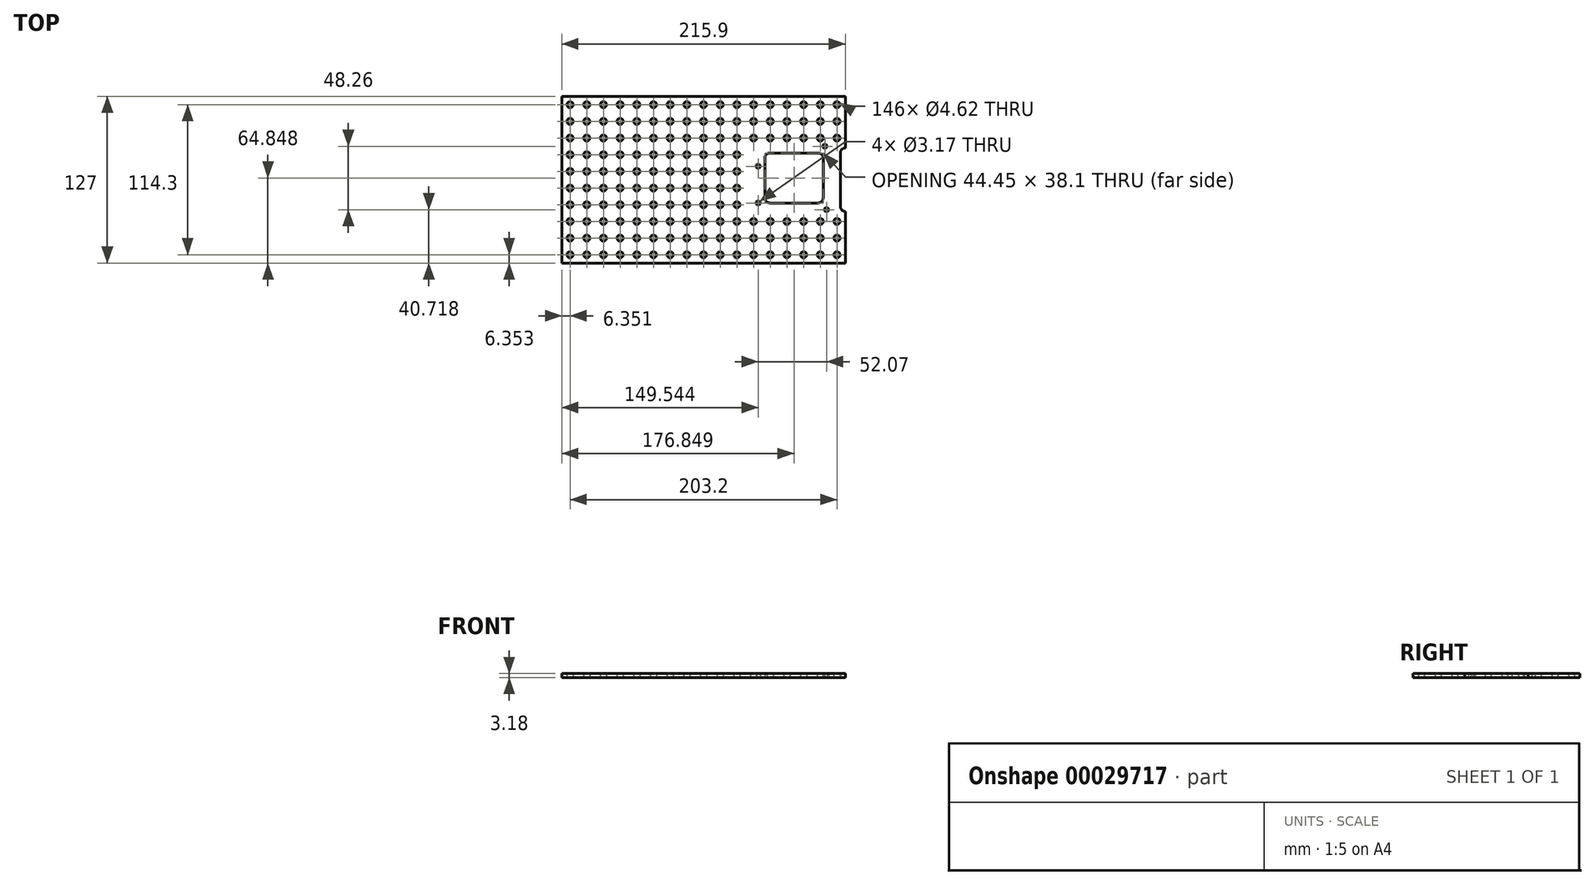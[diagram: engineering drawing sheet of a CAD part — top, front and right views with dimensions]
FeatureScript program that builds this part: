
annotation { "Feature Type Name" : "Feature", "Feature Type Description" : "" }
export const myFeature = defineFeature(function(context is Context, id is Id, definition is map)
    precondition{}
    {
        {
            var Q0;
            Q0=qCreatedBy(makeId("Top.planeOp"),FACE);
            var sketch = newSketch(context, id + "F0", { "sketchPlane" : qUnion([Q0])});
            skLineSegment(sketch, "E0.bottom", {"start": v(-98.48, 59.36) * mm, "end": v(117.42, 59.36) * mm});
            skLineSegment(sketch, "E0.top", {"start": v(-98.48, -67.64) * mm, "end": v(113.61, -67.64) * mm});
            skLineSegment(sketch, "E0.left", {"start": v(-98.48, 59.36) * mm, "end": v(-98.48, -67.64) * mm});
            skLineSegment(sketch, "E0.right", {"start": v(117.42, 59.36) * mm, "end": v(117.42, -63.83) * mm});
            skCircle(sketch, "E1.MirrorC", {"center": v(51.06, -21.84) * mm, "radius": 1.59 * mm});
            skCircle(sketch, "E2.MirrorC", {"center": v(51.06, 6.1) * mm, "radius": 1.59 * mm});
            skCircle(sketch, "E3.MirrorC", {"center": v(103.13, -26.92) * mm, "radius": 1.59 * mm});
            skCircle(sketch, "E4.MirrorC", {"center": v(101.86, 21.34) * mm, "radius": 1.59 * mm});
            skCircle(sketch, "E5", {"center": v(-92.13, 53.01) * mm, "radius": 2.31 * mm});
            skCircle(sketch, "E6.1.0.0", {"center": v(-79.43, 53.01) * mm, "radius": 2.31 * mm});
            skCircle(sketch, "E6.2.0.0", {"center": v(-66.73, 53.01) * mm, "radius": 2.31 * mm});
            skCircle(sketch, "E6.3.0.0", {"center": v(-54.03, 53.01) * mm, "radius": 2.31 * mm});
            skCircle(sketch, "E6.4.0.0", {"center": v(-41.33, 53.01) * mm, "radius": 2.31 * mm});
            skCircle(sketch, "E6.5.0.0", {"center": v(-28.63, 53.01) * mm, "radius": 2.31 * mm});
            skCircle(sketch, "E6.6.0.0", {"center": v(-15.93, 53.01) * mm, "radius": 2.31 * mm});
            skCircle(sketch, "E6.7.0.0", {"center": v(-3.23, 53.01) * mm, "radius": 2.31 * mm});
            skCircle(sketch, "E6.8.0.0", {"center": v(9.47, 53.01) * mm, "radius": 2.31 * mm});
            skCircle(sketch, "E6.9.0.0", {"center": v(22.17, 53.01) * mm, "radius": 2.31 * mm});
            skLineSegment(sketch, "E6.direction1", {"start": v(-92.13, 53.01) * mm, "end": v(-79.43, 53.01) * mm, "construction": true});
            skCircle(sketch, "E7.1.0.0", {"center": v(-92.13, 40.31) * mm, "radius": 2.31 * mm});
            skCircle(sketch, "E7.1.0.1", {"center": v(-79.43, 40.31) * mm, "radius": 2.31 * mm});
            skCircle(sketch, "E7.1.0.2", {"center": v(-66.73, 40.31) * mm, "radius": 2.31 * mm});
            skCircle(sketch, "E7.1.0.3", {"center": v(-3.23, 40.31) * mm, "radius": 2.31 * mm});
            skCircle(sketch, "E7.1.0.4", {"center": v(-15.93, 40.31) * mm, "radius": 2.31 * mm});
            skCircle(sketch, "E7.1.0.5", {"center": v(22.17, 40.31) * mm, "radius": 2.31 * mm});
            skCircle(sketch, "E7.1.0.6", {"center": v(-28.63, 40.31) * mm, "radius": 2.31 * mm});
            skCircle(sketch, "E7.1.0.7", {"center": v(-41.33, 40.31) * mm, "radius": 2.31 * mm});
            skCircle(sketch, "E7.1.0.8", {"center": v(9.47, 40.31) * mm, "radius": 2.31 * mm});
            skLineSegment(sketch, "E7.1.0.9", {"start": v(-92.13, 40.31) * mm, "end": v(-79.43, 40.31) * mm, "construction": true});
            skCircle(sketch, "E7.1.0.10", {"center": v(-54.03, 40.31) * mm, "radius": 2.31 * mm});
            skCircle(sketch, "E7.2.0.0", {"center": v(-92.13, 27.61) * mm, "radius": 2.31 * mm});
            skCircle(sketch, "E7.2.0.1", {"center": v(-79.43, 27.61) * mm, "radius": 2.31 * mm});
            skCircle(sketch, "E7.2.0.2", {"center": v(-66.73, 27.61) * mm, "radius": 2.31 * mm});
            skCircle(sketch, "E7.2.0.3", {"center": v(-3.23, 27.61) * mm, "radius": 2.31 * mm});
            skCircle(sketch, "E7.2.0.4", {"center": v(-15.93, 27.61) * mm, "radius": 2.31 * mm});
            skCircle(sketch, "E7.2.0.5", {"center": v(22.17, 27.61) * mm, "radius": 2.31 * mm});
            skCircle(sketch, "E7.2.0.6", {"center": v(-28.63, 27.61) * mm, "radius": 2.31 * mm});
            skCircle(sketch, "E7.2.0.7", {"center": v(-41.33, 27.61) * mm, "radius": 2.31 * mm});
            skCircle(sketch, "E7.2.0.8", {"center": v(9.47, 27.61) * mm, "radius": 2.31 * mm});
            skLineSegment(sketch, "E7.2.0.9", {"start": v(-92.13, 27.61) * mm, "end": v(-79.43, 27.61) * mm, "construction": true});
            skCircle(sketch, "E7.2.0.10", {"center": v(-54.03, 27.61) * mm, "radius": 2.31 * mm});
            skCircle(sketch, "E7.3.0.0", {"center": v(-92.13, 14.91) * mm, "radius": 2.31 * mm});
            skCircle(sketch, "E7.3.0.1", {"center": v(-79.43, 14.91) * mm, "radius": 2.31 * mm});
            skCircle(sketch, "E7.3.0.2", {"center": v(-66.73, 14.91) * mm, "radius": 2.31 * mm});
            skCircle(sketch, "E7.3.0.3", {"center": v(-3.23, 14.91) * mm, "radius": 2.31 * mm});
            skCircle(sketch, "E7.3.0.4", {"center": v(-15.93, 14.91) * mm, "radius": 2.31 * mm});
            skCircle(sketch, "E7.3.0.5", {"center": v(22.17, 14.91) * mm, "radius": 2.31 * mm});
            skCircle(sketch, "E7.3.0.6", {"center": v(-28.63, 14.91) * mm, "radius": 2.31 * mm});
            skCircle(sketch, "E7.3.0.7", {"center": v(-41.33, 14.91) * mm, "radius": 2.31 * mm});
            skCircle(sketch, "E7.3.0.8", {"center": v(9.47, 14.91) * mm, "radius": 2.31 * mm});
            skLineSegment(sketch, "E7.3.0.9", {"start": v(-92.13, 14.91) * mm, "end": v(-79.43, 14.91) * mm, "construction": true});
            skCircle(sketch, "E7.3.0.10", {"center": v(-54.03, 14.91) * mm, "radius": 2.31 * mm});
            skCircle(sketch, "E7.4.0.0", {"center": v(-92.13, 2.21) * mm, "radius": 2.31 * mm});
            skCircle(sketch, "E7.4.0.1", {"center": v(-79.43, 2.21) * mm, "radius": 2.31 * mm});
            skCircle(sketch, "E7.4.0.2", {"center": v(-66.73, 2.21) * mm, "radius": 2.31 * mm});
            skCircle(sketch, "E7.4.0.3", {"center": v(-3.23, 2.21) * mm, "radius": 2.31 * mm});
            skCircle(sketch, "E7.4.0.4", {"center": v(-15.93, 2.21) * mm, "radius": 2.31 * mm});
            skCircle(sketch, "E7.4.0.5", {"center": v(22.17, 2.21) * mm, "radius": 2.31 * mm});
            skCircle(sketch, "E7.4.0.6", {"center": v(-28.63, 2.21) * mm, "radius": 2.31 * mm});
            skCircle(sketch, "E7.4.0.7", {"center": v(-41.33, 2.21) * mm, "radius": 2.31 * mm});
            skCircle(sketch, "E7.4.0.8", {"center": v(9.47, 2.21) * mm, "radius": 2.31 * mm});
            skLineSegment(sketch, "E7.4.0.9", {"start": v(-92.13, 2.21) * mm, "end": v(-79.43, 2.21) * mm, "construction": true});
            skCircle(sketch, "E7.4.0.10", {"center": v(-54.03, 2.21) * mm, "radius": 2.31 * mm});
            skCircle(sketch, "E7.5.0.0", {"center": v(-92.13, -10.49) * mm, "radius": 2.31 * mm});
            skCircle(sketch, "E7.5.0.1", {"center": v(-79.43, -10.49) * mm, "radius": 2.31 * mm});
            skCircle(sketch, "E7.5.0.2", {"center": v(-66.73, -10.49) * mm, "radius": 2.31 * mm});
            skCircle(sketch, "E7.5.0.3", {"center": v(-3.23, -10.49) * mm, "radius": 2.31 * mm});
            skCircle(sketch, "E7.5.0.4", {"center": v(-15.93, -10.49) * mm, "radius": 2.31 * mm});
            skCircle(sketch, "E7.5.0.5", {"center": v(22.17, -10.49) * mm, "radius": 2.31 * mm});
            skCircle(sketch, "E7.5.0.6", {"center": v(-28.63, -10.49) * mm, "radius": 2.31 * mm});
            skCircle(sketch, "E7.5.0.7", {"center": v(-41.33, -10.49) * mm, "radius": 2.31 * mm});
            skCircle(sketch, "E7.5.0.8", {"center": v(9.47, -10.49) * mm, "radius": 2.31 * mm});
            skLineSegment(sketch, "E7.5.0.9", {"start": v(-92.13, -10.49) * mm, "end": v(-79.43, -10.49) * mm, "construction": true});
            skCircle(sketch, "E7.5.0.10", {"center": v(-54.03, -10.49) * mm, "radius": 2.31 * mm});
            skCircle(sketch, "E7.6.0.0", {"center": v(-92.13, -23.19) * mm, "radius": 2.31 * mm});
            skCircle(sketch, "E7.6.0.1", {"center": v(-79.43, -23.19) * mm, "radius": 2.31 * mm});
            skCircle(sketch, "E7.6.0.2", {"center": v(-66.73, -23.19) * mm, "radius": 2.31 * mm});
            skCircle(sketch, "E7.6.0.3", {"center": v(-3.23, -23.19) * mm, "radius": 2.31 * mm});
            skCircle(sketch, "E7.6.0.4", {"center": v(-15.93, -23.19) * mm, "radius": 2.31 * mm});
            skCircle(sketch, "E7.6.0.5", {"center": v(22.17, -23.19) * mm, "radius": 2.31 * mm});
            skCircle(sketch, "E7.6.0.6", {"center": v(-28.63, -23.19) * mm, "radius": 2.31 * mm});
            skCircle(sketch, "E7.6.0.7", {"center": v(-41.33, -23.19) * mm, "radius": 2.31 * mm});
            skCircle(sketch, "E7.6.0.8", {"center": v(9.47, -23.19) * mm, "radius": 2.31 * mm});
            skLineSegment(sketch, "E7.6.0.9", {"start": v(-92.13, -23.19) * mm, "end": v(-79.43, -23.19) * mm, "construction": true});
            skCircle(sketch, "E7.6.0.10", {"center": v(-54.03, -23.19) * mm, "radius": 2.31 * mm});
            skCircle(sketch, "E7.7.0.0", {"center": v(-92.13, -35.89) * mm, "radius": 2.31 * mm});
            skCircle(sketch, "E7.7.0.1", {"center": v(-79.43, -35.89) * mm, "radius": 2.31 * mm});
            skCircle(sketch, "E7.7.0.2", {"center": v(-66.73, -35.89) * mm, "radius": 2.31 * mm});
            skCircle(sketch, "E7.7.0.3", {"center": v(-3.23, -35.89) * mm, "radius": 2.31 * mm});
            skCircle(sketch, "E7.7.0.4", {"center": v(-15.93, -35.89) * mm, "radius": 2.31 * mm});
            skCircle(sketch, "E7.7.0.5", {"center": v(22.17, -35.89) * mm, "radius": 2.31 * mm});
            skCircle(sketch, "E7.7.0.6", {"center": v(-28.63, -35.89) * mm, "radius": 2.31 * mm});
            skCircle(sketch, "E7.7.0.7", {"center": v(-41.33, -35.89) * mm, "radius": 2.31 * mm});
            skCircle(sketch, "E7.7.0.8", {"center": v(9.47, -35.89) * mm, "radius": 2.31 * mm});
            skLineSegment(sketch, "E7.7.0.9", {"start": v(-92.13, -35.89) * mm, "end": v(-79.43, -35.89) * mm, "construction": true});
            skCircle(sketch, "E7.7.0.10", {"center": v(-54.03, -35.89) * mm, "radius": 2.31 * mm});
            skLineSegment(sketch, "E7.direction1", {"start": v(-92.13, 53.01) * mm, "end": v(-92.13, 40.31) * mm, "construction": true});
            skCircle(sketch, "E8.0.8.0", {"center": v(-92.13, -48.59) * mm, "radius": 2.31 * mm});
            skCircle(sketch, "E8.2.8.0", {"center": v(-79.43, -48.59) * mm, "radius": 2.31 * mm});
            skCircle(sketch, "E8.4.8.0", {"center": v(-66.73, -48.59) * mm, "radius": 2.31 * mm});
            skCircle(sketch, "E8.6.8.0", {"center": v(-3.23, -48.59) * mm, "radius": 2.31 * mm});
            skCircle(sketch, "E8.8.8.0", {"center": v(-15.93, -48.59) * mm, "radius": 2.31 * mm});
            skCircle(sketch, "E8.10.8.0", {"center": v(22.17, -48.59) * mm, "radius": 2.31 * mm});
            skCircle(sketch, "E8.12.8.0", {"center": v(-28.63, -48.59) * mm, "radius": 2.31 * mm});
            skCircle(sketch, "E8.14.8.0", {"center": v(-41.33, -48.59) * mm, "radius": 2.31 * mm});
            skCircle(sketch, "E8.16.8.0", {"center": v(9.47, -48.59) * mm, "radius": 2.31 * mm});
            skLineSegment(sketch, "E8.18.8.0", {"start": v(-92.13, -48.59) * mm, "end": v(-79.43, -48.59) * mm, "construction": true});
            skCircle(sketch, "E8.21.8.0", {"center": v(-54.03, -48.59) * mm, "radius": 2.31 * mm});
            skCircle(sketch, "E8.0.9.0", {"center": v(-92.13, -61.29) * mm, "radius": 2.31 * mm});
            skCircle(sketch, "E8.2.9.0", {"center": v(-79.43, -61.29) * mm, "radius": 2.31 * mm});
            skCircle(sketch, "E8.4.9.0", {"center": v(-66.73, -61.29) * mm, "radius": 2.31 * mm});
            skCircle(sketch, "E8.6.9.0", {"center": v(-3.23, -61.29) * mm, "radius": 2.31 * mm});
            skCircle(sketch, "E8.8.9.0", {"center": v(-15.93, -61.29) * mm, "radius": 2.31 * mm});
            skCircle(sketch, "E8.10.9.0", {"center": v(22.17, -61.29) * mm, "radius": 2.31 * mm});
            skCircle(sketch, "E8.12.9.0", {"center": v(-28.63, -61.29) * mm, "radius": 2.31 * mm});
            skCircle(sketch, "E8.14.9.0", {"center": v(-41.33, -61.29) * mm, "radius": 2.31 * mm});
            skCircle(sketch, "E8.16.9.0", {"center": v(9.47, -61.29) * mm, "radius": 2.31 * mm});
            skLineSegment(sketch, "E8.18.9.0", {"start": v(-92.13, -61.29) * mm, "end": v(-79.43, -61.29) * mm, "construction": true});
            skCircle(sketch, "E8.21.9.0", {"center": v(-54.03, -61.29) * mm, "radius": 2.31 * mm});
            skCircle(sketch, "E9.1.0.0", {"center": v(34.87, 53.01) * mm, "radius": 2.31 * mm});
            skCircle(sketch, "E9.1.0.1", {"center": v(34.87, 40.31) * mm, "radius": 2.31 * mm});
            skCircle(sketch, "E9.2.0.0", {"center": v(47.57, 53.01) * mm, "radius": 2.31 * mm});
            skCircle(sketch, "E9.2.0.1", {"center": v(47.57, 40.31) * mm, "radius": 2.31 * mm});
            skCircle(sketch, "E9.3.0.0", {"center": v(60.27, 53.01) * mm, "radius": 2.31 * mm});
            skCircle(sketch, "E9.3.0.1", {"center": v(60.27, 40.31) * mm, "radius": 2.31 * mm});
            skCircle(sketch, "E9.4.0.0", {"center": v(72.97, 53.01) * mm, "radius": 2.31 * mm});
            skCircle(sketch, "E9.4.0.1", {"center": v(72.97, 40.31) * mm, "radius": 2.31 * mm});
            skCircle(sketch, "E9.5.0.0", {"center": v(85.67, 53.01) * mm, "radius": 2.31 * mm});
            skCircle(sketch, "E9.5.0.1", {"center": v(85.67, 40.31) * mm, "radius": 2.31 * mm});
            skCircle(sketch, "E9.6.0.0", {"center": v(98.37, 53.01) * mm, "radius": 2.31 * mm});
            skCircle(sketch, "E9.6.0.1", {"center": v(98.37, 40.31) * mm, "radius": 2.31 * mm});
            skCircle(sketch, "E9.7.0.0", {"center": v(111.07, 53.01) * mm, "radius": 2.31 * mm});
            skCircle(sketch, "E9.7.0.1", {"center": v(111.07, 40.31) * mm, "radius": 2.31 * mm});
            skLineSegment(sketch, "E9.direction1", {"start": v(22.17, 53.01) * mm, "end": v(34.87, 53.01) * mm, "construction": true});
            skCircle(sketch, "E10.1.0.0", {"center": v(34.87, -48.59) * mm, "radius": 2.31 * mm});
            skCircle(sketch, "E10.1.0.1", {"center": v(34.87, -61.29) * mm, "radius": 2.31 * mm});
            skCircle(sketch, "E10.2.0.0", {"center": v(47.57, -48.59) * mm, "radius": 2.31 * mm});
            skCircle(sketch, "E10.2.0.1", {"center": v(47.57, -61.29) * mm, "radius": 2.31 * mm});
            skCircle(sketch, "E10.3.0.0", {"center": v(60.27, -48.59) * mm, "radius": 2.31 * mm});
            skCircle(sketch, "E10.3.0.1", {"center": v(60.27, -61.29) * mm, "radius": 2.31 * mm});
            skCircle(sketch, "E10.4.0.0", {"center": v(72.97, -48.59) * mm, "radius": 2.31 * mm});
            skCircle(sketch, "E10.4.0.1", {"center": v(72.97, -61.29) * mm, "radius": 2.31 * mm});
            skCircle(sketch, "E10.5.0.0", {"center": v(85.67, -48.59) * mm, "radius": 2.31 * mm});
            skCircle(sketch, "E10.5.0.1", {"center": v(85.67, -61.29) * mm, "radius": 2.31 * mm});
            skCircle(sketch, "E10.6.0.0", {"center": v(98.37, -48.59) * mm, "radius": 2.31 * mm});
            skCircle(sketch, "E10.6.0.1", {"center": v(98.37, -61.29) * mm, "radius": 2.31 * mm});
            skCircle(sketch, "E10.7.0.0", {"center": v(111.07, -48.59) * mm, "radius": 2.31 * mm});
            skCircle(sketch, "E10.7.0.1", {"center": v(111.07, -61.29) * mm, "radius": 2.31 * mm});
            skLineSegment(sketch, "E10.direction1", {"start": v(22.17, -48.59) * mm, "end": v(34.87, -48.59) * mm, "construction": true});
            skCircle(sketch, "E11.1.0.0", {"center": v(34.87, -35.89) * mm, "radius": 2.31 * mm});
            skCircle(sketch, "E11.1.0.1", {"center": v(34.87, 27.61) * mm, "radius": 2.31 * mm});
            skCircle(sketch, "E11.1.0.2", {"center": v(34.87, -10.49) * mm, "radius": 2.31 * mm});
            skCircle(sketch, "E11.1.0.3", {"center": v(34.87, 14.91) * mm, "radius": 2.31 * mm});
            skCircle(sketch, "E11.1.0.4", {"center": v(34.87, -23.19) * mm, "radius": 2.31 * mm});
            skCircle(sketch, "E11.1.0.5", {"center": v(34.87, 2.21) * mm, "radius": 2.31 * mm});
            skLineSegment(sketch, "E11.direction1", {"start": v(22.17, -35.89) * mm, "end": v(34.87, -35.89) * mm, "construction": true});
            skCircle(sketch, "E12.1.0.0", {"center": v(47.57, 27.61) * mm, "radius": 2.31 * mm});
            skCircle(sketch, "E12.1.0.1", {"center": v(111.07, 27.61) * mm, "radius": 2.31 * mm});
            skCircle(sketch, "E12.1.0.2", {"center": v(60.27, 27.61) * mm, "radius": 2.31 * mm});
            skCircle(sketch, "E12.1.0.3", {"center": v(72.97, 27.61) * mm, "radius": 2.31 * mm});
            skCircle(sketch, "E12.1.0.4", {"center": v(85.67, 27.61) * mm, "radius": 2.31 * mm});
            skCircle(sketch, "E12.1.0.5", {"center": v(98.37, 27.61) * mm, "radius": 2.31 * mm});
            skLineSegment(sketch, "E12.direction1", {"start": v(47.57, 40.31) * mm, "end": v(47.57, 27.61) * mm, "construction": true});
            skCircle(sketch, "E13.1.0.0", {"center": v(72.97, -35.89) * mm, "radius": 2.31 * mm});
            skCircle(sketch, "E13.1.0.1", {"center": v(85.67, -35.89) * mm, "radius": 2.31 * mm});
            skCircle(sketch, "E13.1.0.2", {"center": v(98.37, -35.89) * mm, "radius": 2.31 * mm});
            skCircle(sketch, "E13.1.0.3", {"center": v(47.57, -35.89) * mm, "radius": 2.31 * mm});
            skCircle(sketch, "E13.1.0.4", {"center": v(60.27, -35.89) * mm, "radius": 2.31 * mm});
            skCircle(sketch, "E13.1.0.5", {"center": v(111.07, -35.89) * mm, "radius": 2.31 * mm});
            skLineSegment(sketch, "E13.direction1", {"start": v(72.97, -48.59) * mm, "end": v(72.97, -35.89) * mm, "construction": true});
            skLineSegment(sketch, "E14.bottom", {"start": v(117.42, -28.27) * mm, "end": v(117.42, -28.27) * mm});
            skLineSegment(sketch, "E14.top", {"start": v(117.42, 20) * mm, "end": v(117.42, 20) * mm});
            skLineSegment(sketch, "E14.left", {"start": v(117.42, -28.27) * mm, "end": v(117.42, 20) * mm});
            skLineSegment(sketch, "E14.right", {"start": v(113.61, -24.46) * mm, "end": v(113.61, 16.18) * mm});
            skPoint(sketch, "E15.visualSharp", {"position": v(117.42, -67.64) * mm});
            skPoint(sketch, "E16.visualSharp", {"position": v(113.61, -28.27) * mm});
            skArc(sketch, "E16.filletArc", {"start": v(113.61, -24.46) * mm, "mid": v(114.73, -27.15) * mm, "end": v(117.42, -28.27) * mm});
            skPoint(sketch, "E17.visualSharp", {"position": v(113.61, 20) * mm});
            skArc(sketch, "E17.filletArc", {"start": v(117.42, 20) * mm, "mid": v(114.73, 18.88) * mm, "end": v(113.61, 16.18) * mm});
            skLineSegment(sketch, "E18", {"start": v(113.61, -67.64) * mm, "end": v(117.42, -67.64) * mm});
            skLineSegment(sketch, "E19", {"start": v(117.42, -63.83) * mm, "end": v(117.42, -67.64) * mm});
            skLineSegment(sketch, "E20.bottom", {"start": v(59.95, 16.26) * mm, "end": v(96.78, 16.26) * mm});
            skLineSegment(sketch, "E20.top", {"start": v(59.95, -21.84) * mm, "end": v(96.78, -21.84) * mm});
            skLineSegment(sketch, "E20.left", {"start": v(56.14, 12.45) * mm, "end": v(56.14, -18.03) * mm});
            skLineSegment(sketch, "E20.right", {"start": v(100.6, 12.45) * mm, "end": v(100.6, -18.03) * mm});
            skPoint(sketch, "E21.visualSharp", {"position": v(56.14, 16.26) * mm});
            skArc(sketch, "E21.filletArc", {"start": v(59.95, 16.26) * mm, "mid": v(57.26, 15.14) * mm, "end": v(56.14, 12.45) * mm});
            skPoint(sketch, "E22.visualSharp", {"position": v(56.14, -21.84) * mm});
            skArc(sketch, "E22.filletArc", {"start": v(56.14, -18.03) * mm, "mid": v(57.26, -20.73) * mm, "end": v(59.95, -21.84) * mm});
            skPoint(sketch, "E23.visualSharp", {"position": v(100.6, -21.84) * mm});
            skArc(sketch, "E23.filletArc", {"start": v(96.78, -21.84) * mm, "mid": v(99.48, -20.73) * mm, "end": v(100.6, -18.03) * mm});
            skPoint(sketch, "E24.visualSharp", {"position": v(100.6, 16.26) * mm});
            skArc(sketch, "E24.filletArc", {"start": v(100.6, 12.45) * mm, "mid": v(99.48, 15.14) * mm, "end": v(96.78, 16.26) * mm});
            skSolve(sketch);
        }
        {
            var Q0;
            Q0=makeQuery(id+"F0.imprint","IMPRINT",FACE,{"disambiguationData":[TD([[makeQuery(id+"F0.imprint","IMPRINT",EDGE,{"derivedFrom":sQuery(id+"F0.wireOp",EDGE,"E0.bottom")}),-1.0]])]});
            extrude(context, id + "F1", {"entities" : qUnion([Q0]), "depth" : 3.17 * mm});
        }
    });
